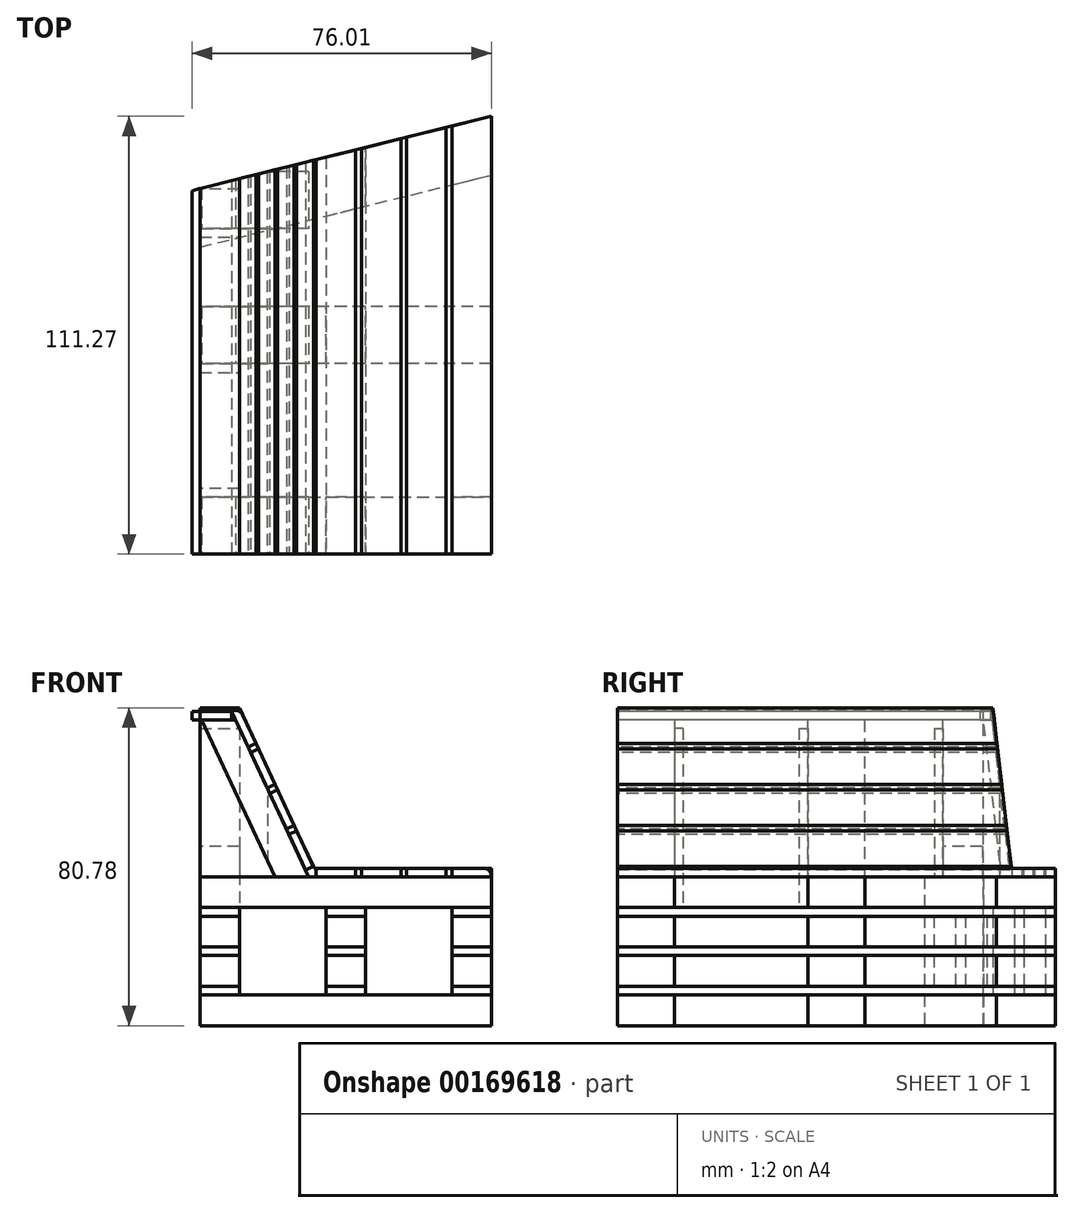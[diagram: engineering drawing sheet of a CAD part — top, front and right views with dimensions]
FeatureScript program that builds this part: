
annotation { "Feature Type Name" : "Feature", "Feature Type Description" : "" }
export const myFeature = defineFeature(function(context is Context, id is Id, definition is map)
    precondition{}
    {
        {
            assignVariable(context, id + "F0", {"name" : "h1", "anyValue" : 7.8});
        }
        {
            assignVariable(context, id + "F1", {"name" : "h2", "anyValue" : 2.2});
        }
        {
            assignVariable(context, id + "F2", {"name" : "b1", "anyValue" : 14.5});
        }
        {
            assignVariable(context, id + "F3", {"name" : "b2", "anyValue" : 10});
        }
        {
            var Q0;
            Q0=qCreatedBy(makeId("Top.planeOp"),FACE);
            var sketch = newSketch(context, id + "F4", { "sketchPlane" : qUnion([Q0])});
            skLineSegment(sketch, "E0", {"start": v(0, 0) * mm, "end": v(-33, 0) * mm});
            skLineSegment(sketch, "E1", {"start": v(-33, 0) * mm, "end": v(-33, 90) * mm});
            skLineSegment(sketch, "E2", {"start": v(0, 0) * mm, "end": v(0, -3) * mm});
            skLineSegment(sketch, "E3", {"start": v(0, -3) * mm, "end": v(42, -3) * mm});
            skLineSegment(sketch, "E4", {"start": v(42, -3) * mm, "end": v(50, -11) * mm});
            skLineSegment(sketch, "E5", {"start": v(50, -11) * mm, "end": v(85, -11) * mm});
            skLineSegment(sketch, "E6", {"start": v(0, 0) * mm, "end": v(0, 100) * mm, "construction": true});
            skLineSegment(sketch, "E7", {"start": v(42, -3) * mm, "end": v(42, 110) * mm, "construction": true});
            skFitSpline(sketch, "E8", {"points": [v(-33, 90) * mm, v(0, 100) * mm, v(42, 110) * mm, v(85, 115) * mm], "startDerivative": vector(155.67, 52.1) * mm, "endDerivative": vector(124.82, 12.6) * mm});
            skLineSegment(sketch, "E9", {"start": v(85, 115) * mm, "end": v(85, -11) * mm, "construction": true});
            skSolve(sketch);
        }
        {
            var Q0;
            Q0=sQuery(id+"F4.wireOp",EDGE,"E8");
            var Q1;
            Q1=sQuery(id+"F4.wireOp",EDGE,"E1");
            var Q2;
            Q2=sQuery(id+"F4.wireOp",EDGE,"E0");
            var Q3;
            Q3=sQuery(id+"F4.wireOp",EDGE,"E2");
            var Q4;
            Q4=sQuery(id+"F4.wireOp",EDGE,"E3");
            var Q5;
            Q5=sQuery(id+"F4.wireOp",EDGE,"E4");
            var Q6;
            Q6=sQuery(id+"F4.wireOp",EDGE,"E5");
            extrude(context, id + "F5", {"bodyType" : ToolBodyType.SURFACE, "surfaceEntities" : qUnion([Q0, Q1, Q2, Q3, Q4, Q5, Q6]), "depth" : 92 * mm});
        }
        {
            var Q0;
            Q0=qCreatedBy(makeId("Front.planeOp"),FACE);
            var sketch = newSketch(context, id + "F6", { "sketchPlane" : qUnion([Q0])});
            skLineSegment(sketch, "E10", {"start": v(-24.02, 0) * mm, "end": v(50, 0) * mm});
            skLineSegment(sketch, "E11", {"start": v(50, 0) * mm, "end": v(50, 40) * mm});
            skLineSegment(sketch, "E12", {"start": v(50, 40) * mm, "end": v(5, 40) * mm});
            skLineSegment(sketch, "E13", {"start": v(5, 40) * mm, "end": v(-14.02, 80.78) * mm});
            skLineSegment(sketch, "E14", {"start": v(-14.02, 80.78) * mm, "end": v(-24.02, 80.78) * mm});
            skLineSegment(sketch, "E15", {"start": v(-24.02, 80.78) * mm, "end": v(-24.02, 0) * mm});
            skSolve(sketch);
        }
        {
            var Q0;
            Q0 = qSketchRegion(id + "F6", true);
            var Q1;
            Q1=makeQuery(id+"F5.opExtrude","SWEPT_FACE",FACE,{"disambiguationData":[OSD([sQuery(id+"F4.wireOp",EDGE,"E8")])]});
            extrude(context, id + "F7", {"entities" : qUnion([Q0]), "endBound" : BoundingType.UP_TO_SURFACE, "oppositeDirection" : true, "endBoundEntityFace" : qUnion([Q1]), "depth" : 25 * mm});
        }
        {
            var Q0;
            Q0=qCreatedBy(makeId("Top.planeOp"),FACE);
            var sketch = newSketch(context, id + "F8", { "sketchPlane" : qUnion([Q0])});
            skLineSegment(sketch, "E16.bottom", {"start": v(-24.02, 0) * mm, "end": v(50, 0) * mm});
            skLineSegment(sketch, "E16.top", {"start": v(-24.02, 14.5) * mm, "end": v(50, 14.5) * mm});
            skLineSegment(sketch, "E16.left", {"start": v(-24.02, 0) * mm, "end": v(-24.02, 14.5) * mm});
            skLineSegment(sketch, "E16.right", {"start": v(50, 0) * mm, "end": v(50, 14.5) * mm});
            skLineSegment(sketch, "E17", {"start": v(-24.02, 92.95) * mm, "end": v(-24.02, 78.02) * mm});
            skLineSegment(sketch, "E18", {"start": v(-24.02, 78.02) * mm, "end": v(50, 96.34) * mm});
            skLineSegment(sketch, "E19", {"start": v(50, 96.34) * mm, "end": v(50, 111.27) * mm});
            skLineSegment(sketch, "E20", {"start": v(50, 111.27) * mm, "end": v(-24.02, 92.95) * mm});
            skLineSegment(sketch, "E21.bottom", {"start": v(50, 62.89) * mm, "end": v(-24.02, 62.89) * mm});
            skLineSegment(sketch, "E21.top", {"start": v(50, 48.39) * mm, "end": v(-24.02, 48.39) * mm});
            skLineSegment(sketch, "E21.left", {"start": v(50, 62.89) * mm, "end": v(50, 48.39) * mm});
            skLineSegment(sketch, "E21.right", {"start": v(-24.02, 62.89) * mm, "end": v(-24.02, 48.39) * mm});
            skPoint(sketch, "E21.middle", {"position": v(13, 55.64) * mm});
            skPoint(sketch, "E22", {"position": v(50, 55.64) * mm});
            skSolve(sketch);
        }
        {
            var Q0;
            Q0 = qSketchRegion(id + "F8", true);
            extrude(context, id + "F9", {"entities" : qUnion([Q0]), "depth" : (getVariable(context, 'h1')) * mm});
        }
        {
            var Q0;
            Q0=qCreatedBy(makeId("Front.planeOp"),FACE);
            var sketch = newSketch(context, id + "F10", { "sketchPlane" : qUnion([Q0])});
            skLineSegment(sketch, "E23.bottom", {"start": v(-14.02, 7.8) * mm, "end": v(-24.02, 7.8) * mm});
            skLineSegment(sketch, "E23.top", {"start": v(-14.02, 10) * mm, "end": v(-24.02, 10) * mm});
            skLineSegment(sketch, "E23.left", {"start": v(-14.02, 7.8) * mm, "end": v(-14.02, 10) * mm});
            skLineSegment(sketch, "E23.right", {"start": v(-24.02, 7.8) * mm, "end": v(-24.02, 10) * mm});
            skPoint(sketch, "E23.middle", {"position": v(-19.02, 8.9) * mm});
            skLineSegment(sketch, "E24.bottom", {"start": v(18, 7.8) * mm, "end": v(8, 7.8) * mm});
            skLineSegment(sketch, "E24.top", {"start": v(18, 10) * mm, "end": v(8, 10) * mm});
            skLineSegment(sketch, "E24.left", {"start": v(18, 7.8) * mm, "end": v(18, 10) * mm});
            skLineSegment(sketch, "E24.right", {"start": v(8, 7.8) * mm, "end": v(8, 10) * mm});
            skPoint(sketch, "E24.middle", {"position": v(13, 8.9) * mm});
            skLineSegment(sketch, "E25.bottom", {"start": v(50, 7.8) * mm, "end": v(40, 7.8) * mm});
            skLineSegment(sketch, "E25.top", {"start": v(50, 10) * mm, "end": v(40, 10) * mm});
            skLineSegment(sketch, "E25.left", {"start": v(50, 7.8) * mm, "end": v(50, 10) * mm});
            skLineSegment(sketch, "E25.right", {"start": v(40, 7.8) * mm, "end": v(40, 10) * mm});
            skPoint(sketch, "E25.middle", {"position": v(45, 8.9) * mm});
            skSolve(sketch);
        }
        {
            var Q0;
            Q0 = qSketchRegion(id + "F10", true);
            var Q1;
            Q1=makeQuery(id+"F5.opExtrude","SWEPT_FACE",FACE,{"disambiguationData":[OSD([sQuery(id+"F4.wireOp",EDGE,"E8")])]});
            extrude(context, id + "F11", {"entities" : qUnion([Q0]), "endBound" : BoundingType.UP_TO_SURFACE, "oppositeDirection" : true, "endBoundEntityFace" : qUnion([Q1]), "depth" : 25 * mm});
        }
        {
            var Q0;
            Q0=makeQuery(id+"F11.opExtrude","SWEPT_FACE",FACE,{"disambiguationData":[OSD([sQuery(id+"F10.wireOp",EDGE,"E25.top")])]});
            var sketch = newSketch(context, id + "F12", { "sketchPlane" : qUnion([Q0])});
            skLineSegment(sketch, "E26.bottom", {"start": v(-14.02, 48.39) * mm, "end": v(-24.02, 48.39) * mm});
            skLineSegment(sketch, "E26.top", {"start": v(-14.02, 62.89) * mm, "end": v(-24.02, 62.89) * mm});
            skLineSegment(sketch, "E26.left", {"start": v(-14.02, 48.39) * mm, "end": v(-14.02, 62.89) * mm});
            skLineSegment(sketch, "E26.right", {"start": v(-24.02, 48.39) * mm, "end": v(-24.02, 62.89) * mm});
            skPoint(sketch, "E26.middle", {"position": v(-19.02, 55.64) * mm});
            skLineSegment(sketch, "E27.bottom", {"start": v(18, 48.39) * mm, "end": v(8, 48.39) * mm});
            skLineSegment(sketch, "E27.top", {"start": v(18, 62.89) * mm, "end": v(8, 62.89) * mm});
            skLineSegment(sketch, "E27.left", {"start": v(18, 48.39) * mm, "end": v(18, 62.89) * mm});
            skLineSegment(sketch, "E27.right", {"start": v(8, 48.39) * mm, "end": v(8, 62.89) * mm});
            skPoint(sketch, "E27.middle", {"position": v(13, 55.64) * mm});
            skLineSegment(sketch, "E28.bottom", {"start": v(50, 48.39) * mm, "end": v(40, 48.39) * mm});
            skLineSegment(sketch, "E28.top", {"start": v(50, 62.89) * mm, "end": v(40, 62.89) * mm});
            skLineSegment(sketch, "E28.left", {"start": v(50, 48.39) * mm, "end": v(50, 62.89) * mm});
            skLineSegment(sketch, "E28.right", {"start": v(40, 48.39) * mm, "end": v(40, 62.89) * mm});
            skPoint(sketch, "E28.middle", {"position": v(45, 55.64) * mm});
            skLineSegment(sketch, "E29.bottom", {"start": v(-14.02, 0) * mm, "end": v(-24.02, 0) * mm});
            skLineSegment(sketch, "E29.top", {"start": v(-14.02, 14.5) * mm, "end": v(-24.02, 14.5) * mm});
            skLineSegment(sketch, "E29.left", {"start": v(-14.02, 0) * mm, "end": v(-14.02, 14.5) * mm});
            skLineSegment(sketch, "E29.right", {"start": v(-24.02, 0) * mm, "end": v(-24.02, 14.5) * mm});
            skPoint(sketch, "E29.middle", {"position": v(-19.02, 7.25) * mm});
            skLineSegment(sketch, "E30.bottom", {"start": v(18, 0) * mm, "end": v(8, 0) * mm});
            skLineSegment(sketch, "E30.top", {"start": v(18, 14.5) * mm, "end": v(8, 14.5) * mm});
            skLineSegment(sketch, "E30.left", {"start": v(18, 0) * mm, "end": v(18, 14.5) * mm});
            skLineSegment(sketch, "E30.right", {"start": v(8, 0) * mm, "end": v(8, 14.5) * mm});
            skPoint(sketch, "E30.middle", {"position": v(13, 7.25) * mm});
            skLineSegment(sketch, "E31.bottom", {"start": v(50, 0) * mm, "end": v(40, 0) * mm});
            skLineSegment(sketch, "E31.top", {"start": v(50, 14.5) * mm, "end": v(40, 14.5) * mm});
            skLineSegment(sketch, "E31.left", {"start": v(50, 0) * mm, "end": v(50, 14.5) * mm});
            skLineSegment(sketch, "E31.right", {"start": v(40, 0) * mm, "end": v(40, 14.5) * mm});
            skPoint(sketch, "E31.middle", {"position": v(45, 7.25) * mm});
            skLineSegment(sketch, "E32", {"start": v(-24.02, 78.02) * mm, "end": v(-14.02, 80.5) * mm});
            skLineSegment(sketch, "E33", {"start": v(-14.02, 80.5) * mm, "end": v(-14.02, 95.43) * mm});
            skLineSegment(sketch, "E34", {"start": v(-14.02, 95.43) * mm, "end": v(-24.02, 92.95) * mm});
            skLineSegment(sketch, "E35", {"start": v(-24.02, 92.95) * mm, "end": v(-24.02, 78.02) * mm});
            skLineSegment(sketch, "E36", {"start": v(8, 85.94) * mm, "end": v(18, 88.41) * mm});
            skLineSegment(sketch, "E37", {"start": v(18, 88.41) * mm, "end": v(18, 103.35) * mm});
            skLineSegment(sketch, "E38", {"start": v(18, 103.35) * mm, "end": v(8, 100.88) * mm});
            skLineSegment(sketch, "E39", {"start": v(8, 100.88) * mm, "end": v(8, 85.94) * mm});
            skLineSegment(sketch, "E40", {"start": v(40, 93.86) * mm, "end": v(50, 96.34) * mm});
            skLineSegment(sketch, "E41", {"start": v(50, 96.34) * mm, "end": v(50, 111.27) * mm});
            skLineSegment(sketch, "E42", {"start": v(50, 111.27) * mm, "end": v(40, 108.8) * mm});
            skLineSegment(sketch, "E43", {"start": v(40, 108.8) * mm, "end": v(40, 93.86) * mm});
            skSolve(sketch);
        }
        {
            var Q0;
            Q0=makeQuery(id+"F11.opExtrude","SWEPT_BODY",BODY,{"disambiguationData":[OSD([sQuery(id+"F10.wireOp",EDGE,"E25.bottom"),sQuery(id+"F10.wireOp",EDGE,"E25.top"),sQuery(id+"F10.wireOp",EDGE,"E25.left"),sQuery(id+"F10.wireOp",EDGE,"E25.right")])]});
            var Q1;
            Q1=makeQuery(id+"F11.opExtrude","SWEPT_BODY",BODY,{"disambiguationData":[OSD([sQuery(id+"F10.wireOp",EDGE,"E24.bottom"),sQuery(id+"F10.wireOp",EDGE,"E24.top"),sQuery(id+"F10.wireOp",EDGE,"E24.left"),sQuery(id+"F10.wireOp",EDGE,"E24.right")])]});
            var Q2;
            Q2=makeQuery(id+"F11.opExtrude","SWEPT_BODY",BODY,{"disambiguationData":[OSD([sQuery(id+"F10.wireOp",EDGE,"E23.bottom"),sQuery(id+"F10.wireOp",EDGE,"E23.top"),sQuery(id+"F10.wireOp",EDGE,"E23.left"),sQuery(id+"F10.wireOp",EDGE,"E23.right")])]});
            transform(context, id + "F13", {"entities" : qUnion([Q0, Q1, Q2]), "transformType" : TransformType.TRANSLATION_3D, "dx" : 0 * mm, "dy" : 0 * mm, "dz" : (getVariable(context, 'h1') + getVariable(context, 'h2')) * mm, "makeCopy" : true});
        }
        {
            var Q0;
            Q0=makeQuery(id+"Fk0cpU2CD6sY0ll_8.opPattern","COPY",BODY,{"derivedFrom":makeQuery(id+"F9.opExtrude","SWEPT_BODY",BODY,{"disambiguationData":[OSD([sQuery(id+"F8.wireOp",EDGE,"E16.bottom"),sQuery(id+"F8.wireOp",EDGE,"E16.top"),sQuery(id+"F8.wireOp",EDGE,"E16.left"),sQuery(id+"F8.wireOp",EDGE,"E16.right")])]}),"instanceName":"1"});
            var Q1;
            Q1=makeQuery(id+"Fk0cpU2CD6sY0ll_8.opPattern","COPY",BODY,{"derivedFrom":makeQuery(id+"F9.opExtrude","SWEPT_BODY",BODY,{"disambiguationData":[OSD([sQuery(id+"F8.wireOp",EDGE,"E21.bottom"),sQuery(id+"F8.wireOp",EDGE,"E21.top"),sQuery(id+"F8.wireOp",EDGE,"E21.left"),sQuery(id+"F8.wireOp",EDGE,"E21.right")])]}),"instanceName":"1"});
            var Q2;
            Q2=makeQuery(id+"Fk0cpU2CD6sY0ll_8.opPattern","COPY",BODY,{"derivedFrom":makeQuery(id+"F9.opExtrude","SWEPT_BODY",BODY,{"disambiguationData":[OSD([sQuery(id+"F8.wireOp",EDGE,"E17"),sQuery(id+"F8.wireOp",EDGE,"E18"),sQuery(id+"F8.wireOp",EDGE,"E19"),sQuery(id+"F8.wireOp",EDGE,"E20")])]}),"instanceName":"1"});
            var Q3;
            Q3=makeQuery(id+"F13.opPattern","COPY",BODY,{"derivedFrom":makeQuery(id+"F11.opExtrude","SWEPT_BODY",BODY,{"disambiguationData":[OSD([sQuery(id+"F10.wireOp",EDGE,"E25.bottom"),sQuery(id+"F10.wireOp",EDGE,"E25.top"),sQuery(id+"F10.wireOp",EDGE,"E25.left"),sQuery(id+"F10.wireOp",EDGE,"E25.right")])]}),"instanceName":"1"});
            var Q4;
            Q4=makeQuery(id+"F13.opPattern","COPY",BODY,{"derivedFrom":makeQuery(id+"F11.opExtrude","SWEPT_BODY",BODY,{"disambiguationData":[OSD([sQuery(id+"F10.wireOp",EDGE,"E24.bottom"),sQuery(id+"F10.wireOp",EDGE,"E24.top"),sQuery(id+"F10.wireOp",EDGE,"E24.left"),sQuery(id+"F10.wireOp",EDGE,"E24.right")])]}),"instanceName":"1"});
            var Q5;
            Q5=makeQuery(id+"F13.opPattern","COPY",BODY,{"derivedFrom":makeQuery(id+"F11.opExtrude","SWEPT_BODY",BODY,{"disambiguationData":[OSD([sQuery(id+"F10.wireOp",EDGE,"E23.bottom"),sQuery(id+"F10.wireOp",EDGE,"E23.top"),sQuery(id+"F10.wireOp",EDGE,"E23.left"),sQuery(id+"F10.wireOp",EDGE,"E23.right")])]}),"instanceName":"1"});
            transform(context, id + "F14", {"entities" : qUnion([Q0, Q1, Q2, Q3, Q4, Q5]), "transformType" : TransformType.TRANSLATION_3D, "dx" : 0 * mm, "dy" : 0 * mm, "dz" : (getVariable(context, 'h1') + getVariable(context, 'h2')) * mm, "makeCopy" : true});
        }
        {
            var Q0;
            Q0 = qSketchRegion(id + "F12", true);
            extrude(context, id + "F15", {"entities" : qUnion([Q0]), "depth" : (getVariable(context, 'h1')) * mm});
        }
        {
            var Q0;
            Q0=makeQuery(id+"F15.opExtrude","SWEPT_BODY",BODY,{"disambiguationData":[OSD([sQuery(id+"F12.wireOp",EDGE,"E31.bottom"),sQuery(id+"F12.wireOp",EDGE,"E31.top"),sQuery(id+"F12.wireOp",EDGE,"E31.left"),sQuery(id+"F12.wireOp",EDGE,"E31.right")])]});
            var Q1;
            Q1=makeQuery(id+"F15.opExtrude","SWEPT_BODY",BODY,{"disambiguationData":[OSD([sQuery(id+"F12.wireOp",EDGE,"E30.bottom"),sQuery(id+"F12.wireOp",EDGE,"E30.top"),sQuery(id+"F12.wireOp",EDGE,"E30.left"),sQuery(id+"F12.wireOp",EDGE,"E30.right")])]});
            var Q2;
            Q2=makeQuery(id+"F15.opExtrude","SWEPT_BODY",BODY,{"disambiguationData":[OSD([sQuery(id+"F12.wireOp",EDGE,"E29.bottom"),sQuery(id+"F12.wireOp",EDGE,"E29.top"),sQuery(id+"F12.wireOp",EDGE,"E29.left"),sQuery(id+"F12.wireOp",EDGE,"E29.right")])]});
            var Q3;
            Q3=makeQuery(id+"F15.opExtrude","SWEPT_BODY",BODY,{"disambiguationData":[OSD([sQuery(id+"F12.wireOp",EDGE,"E26.bottom"),sQuery(id+"F12.wireOp",EDGE,"E26.top"),sQuery(id+"F12.wireOp",EDGE,"E26.left"),sQuery(id+"F12.wireOp",EDGE,"E26.right")])]});
            var Q4;
            Q4=makeQuery(id+"F15.opExtrude","SWEPT_BODY",BODY,{"disambiguationData":[OSD([sQuery(id+"F12.wireOp",EDGE,"E27.bottom"),sQuery(id+"F12.wireOp",EDGE,"E27.top"),sQuery(id+"F12.wireOp",EDGE,"E27.left"),sQuery(id+"F12.wireOp",EDGE,"E27.right")])]});
            var Q5;
            Q5=makeQuery(id+"F15.opExtrude","SWEPT_BODY",BODY,{"disambiguationData":[OSD([sQuery(id+"F12.wireOp",EDGE,"E28.bottom"),sQuery(id+"F12.wireOp",EDGE,"E28.top"),sQuery(id+"F12.wireOp",EDGE,"E28.left"),sQuery(id+"F12.wireOp",EDGE,"E28.right")])]});
            var Q6;
            Q6=makeQuery(id+"F15.opExtrude","SWEPT_BODY",BODY,{"disambiguationData":[OSD([sQuery(id+"F12.wireOp",EDGE,"E32"),sQuery(id+"F12.wireOp",EDGE,"E33"),sQuery(id+"F12.wireOp",EDGE,"E34"),sQuery(id+"F12.wireOp",EDGE,"E35")])]});
            var Q7;
            Q7=makeQuery(id+"F15.opExtrude","SWEPT_BODY",BODY,{"disambiguationData":[OSD([sQuery(id+"F12.wireOp",EDGE,"E36"),sQuery(id+"F12.wireOp",EDGE,"E37"),sQuery(id+"F12.wireOp",EDGE,"E38"),sQuery(id+"F12.wireOp",EDGE,"E39")])]});
            var Q8;
            Q8=makeQuery(id+"F15.opExtrude","SWEPT_BODY",BODY,{"disambiguationData":[OSD([sQuery(id+"F12.wireOp",EDGE,"E40"),sQuery(id+"F12.wireOp",EDGE,"E41"),sQuery(id+"F12.wireOp",EDGE,"E42"),sQuery(id+"F12.wireOp",EDGE,"E43")])]});
            transform(context, id + "F16", {"entities" : qUnion([Q0, Q1, Q2, Q3, Q4, Q5, Q6, Q7, Q8]), "transformType" : TransformType.TRANSLATION_3D, "dx" : 0 * mm, "dy" : 0 * mm, "dz" : (getVariable(context, 'h1') + getVariable(context, 'h2')) * mm, "makeCopy" : true});
        }
        {
            var Q0;
            Q0=makeQuery(id+"F9.opExtrude","SWEPT_BODY",BODY,{"disambiguationData":[OSD([sQuery(id+"F8.wireOp",EDGE,"E16.bottom"),sQuery(id+"F8.wireOp",EDGE,"E16.top"),sQuery(id+"F8.wireOp",EDGE,"E16.left"),sQuery(id+"F8.wireOp",EDGE,"E16.right")])]});
            var Q1;
            Q1=makeQuery(id+"F9.opExtrude","SWEPT_BODY",BODY,{"disambiguationData":[OSD([sQuery(id+"F8.wireOp",EDGE,"E21.bottom"),sQuery(id+"F8.wireOp",EDGE,"E21.top"),sQuery(id+"F8.wireOp",EDGE,"E21.left"),sQuery(id+"F8.wireOp",EDGE,"E21.right")])]});
            var Q2;
            Q2=makeQuery(id+"F9.opExtrude","SWEPT_BODY",BODY,{"disambiguationData":[OSD([sQuery(id+"F8.wireOp",EDGE,"E17"),sQuery(id+"F8.wireOp",EDGE,"E18"),sQuery(id+"F8.wireOp",EDGE,"E19"),sQuery(id+"F8.wireOp",EDGE,"E20")])]});
            transform(context, id + "F17", {"entities" : qUnion([Q0, Q1, Q2]), "transformType" : TransformType.TRANSLATION_3D, "dx" : 0 * mm, "dy" : 0 * mm, "dz" : (3 * (getVariable(context, 'h1') + getVariable(context, 'h2'))) * mm, "makeCopy" : true});
        }
        {
            var Q0;
            Q0=qCreatedBy(makeId("Front.planeOp"),FACE);
            var sketch = newSketch(context, id + "F18", { "sketchPlane" : qUnion([Q0])});
            skLineSegment(sketch, "E44.bottom", {"start": v(50, 37.8) * mm, "end": v(40, 37.8) * mm});
            skLineSegment(sketch, "E44.top", {"start": v(50, 40) * mm, "end": v(40, 40) * mm});
            skLineSegment(sketch, "E44.left", {"start": v(50, 37.8) * mm, "end": v(50, 40) * mm});
            skLineSegment(sketch, "E44.right", {"start": v(40, 37.8) * mm, "end": v(40, 40) * mm});
            skLineSegment(sketch, "E45.bottom", {"start": v(38.5, 37.8) * mm, "end": v(28.5, 37.8) * mm});
            skLineSegment(sketch, "E45.top", {"start": v(38.5, 40) * mm, "end": v(28.5, 40) * mm});
            skLineSegment(sketch, "E45.left", {"start": v(38.5, 37.8) * mm, "end": v(38.5, 40) * mm});
            skLineSegment(sketch, "E45.right", {"start": v(28.5, 37.8) * mm, "end": v(28.5, 40) * mm});
            skLineSegment(sketch, "E46.bottom", {"start": v(27, 37.8) * mm, "end": v(17, 37.8) * mm});
            skLineSegment(sketch, "E46.top", {"start": v(27, 40) * mm, "end": v(17, 40) * mm});
            skLineSegment(sketch, "E46.left", {"start": v(27, 37.8) * mm, "end": v(27, 40) * mm});
            skLineSegment(sketch, "E46.right", {"start": v(17, 37.8) * mm, "end": v(17, 40) * mm});
            skLineSegment(sketch, "E47.bottom", {"start": v(5.5, 37.8) * mm, "end": v(15.5, 37.8) * mm});
            skLineSegment(sketch, "E47.top", {"start": v(5.5, 40) * mm, "end": v(15.5, 40) * mm});
            skLineSegment(sketch, "E47.left", {"start": v(5.5, 37.8) * mm, "end": v(5.5, 40) * mm});
            skLineSegment(sketch, "E47.right", {"start": v(15.5, 37.8) * mm, "end": v(15.5, 40) * mm});
            skSolve(sketch);
        }
        {
            var Q0;
            Q0 = qSketchRegion(id + "F18", true);
            var Q1;
            Q1=makeQuery(id+"F5.opExtrude","SWEPT_FACE",FACE,{"disambiguationData":[OSD([sQuery(id+"F4.wireOp",EDGE,"E8")])]});
            extrude(context, id + "F19", {"entities" : qUnion([Q0]), "endBound" : BoundingType.UP_TO_SURFACE, "oppositeDirection" : true, "endBoundEntityFace" : qUnion([Q1]), "depth" : 25 * mm});
        }
        {
            var Q0;
            Q0=qCreatedBy(makeId("Front.planeOp"),FACE);
            var sketch = newSketch(context, id + "F20", { "sketchPlane" : qUnion([Q0])});
            skLineSegment(sketch, "E48", {"start": v(-14.02, 80.78) * mm, "end": v(-9.8, 71.72) * mm});
            skLineSegment(sketch, "E49", {"start": v(-9.8, 71.72) * mm, "end": v(-11.79, 70.8) * mm});
            skLineSegment(sketch, "E50", {"start": v(-11.79, 70.8) * mm, "end": v(-16.01, 79.85) * mm});
            skLineSegment(sketch, "E51", {"start": v(-16.01, 79.85) * mm, "end": v(-14.02, 80.78) * mm});
            skLineSegment(sketch, "E52", {"start": v(-9.16, 70.36) * mm, "end": v(-4.93, 61.3) * mm});
            skLineSegment(sketch, "E53", {"start": v(-4.93, 61.3) * mm, "end": v(-6.93, 60.37) * mm});
            skLineSegment(sketch, "E54", {"start": v(-6.93, 60.37) * mm, "end": v(-11.15, 69.43) * mm});
            skLineSegment(sketch, "E55", {"start": v(-11.15, 69.43) * mm, "end": v(-9.16, 70.36) * mm});
            skLineSegment(sketch, "E56", {"start": v(-6.3, 59) * mm, "end": v(-2.07, 49.95) * mm});
            skLineSegment(sketch, "E57", {"start": v(-2.07, 49.95) * mm, "end": v(-0.07, 50.88) * mm});
            skLineSegment(sketch, "E58", {"start": v(-0.07, 50.88) * mm, "end": v(-4.3, 59.94) * mm});
            skLineSegment(sketch, "E59", {"start": v(-4.3, 59.94) * mm, "end": v(-6.3, 59) * mm});
            skLineSegment(sketch, "E60", {"start": v(0.56, 49.52) * mm, "end": v(4.79, 40.45) * mm});
            skLineSegment(sketch, "E61", {"start": v(4.79, 40.45) * mm, "end": v(2.8, 39.52) * mm});
            skLineSegment(sketch, "E62", {"start": v(2.8, 39.52) * mm, "end": v(-1.43, 48.59) * mm});
            skLineSegment(sketch, "E63", {"start": v(-1.43, 48.59) * mm, "end": v(0.56, 49.52) * mm});
            skSolve(sketch);
        }
        {
            var Q0;
            Q0 = qSketchRegion(id + "F20", true);
            var Q1;
            Q1=makeQuery(id+"F5.opExtrude","SWEPT_FACE",FACE,{"disambiguationData":[OSD([sQuery(id+"F4.wireOp",EDGE,"E8")])]});
            extrude(context, id + "F21", {"entities" : qUnion([Q0]), "endBound" : BoundingType.UP_TO_SURFACE, "oppositeDirection" : true, "endBoundEntityFace" : qUnion([Q1]), "depth" : 25 * mm});
        }
        {
            var Q0;
            Q0=qCreatedBy(makeId("Front.planeOp"),FACE);
            var sketch = newSketch(context, id + "F22", { "sketchPlane" : qUnion([Q0])});
            skLineSegment(sketch, "E64", {"start": v(-5, 37.8) * mm, "end": v(3.6, 37.8) * mm});
            skLineSegment(sketch, "E65", {"start": v(3.6, 37.8) * mm, "end": v(-14.99, 77.65) * mm});
            skLineSegment(sketch, "E66", {"start": v(-14.99, 77.65) * mm, "end": v(-23.6, 77.65) * mm});
            skLineSegment(sketch, "E67", {"start": v(-23.6, 77.65) * mm, "end": v(-5, 37.8) * mm});
            skSolve(sketch);
        }
        {
            var Q0;
            Q0 = qSketchRegion(id + "F22", true);
            extrude(context, id + "F23", {"entities" : qUnion([Q0]), "oppositeDirection" : true, "depth" : (getVariable(context, 'b1')) * mm});
        }
        {
            var Q0;
            Q0=makeQuery(id+"F17.opPattern","COPY",FACE,{"derivedFrom":makeQuery(id+"F9.opExtrude","SWEPT_FACE",FACE,{"disambiguationData":[OSD([sQuery(id+"F8.wireOp",EDGE,"E21.top")])]}),"instanceName":"1"});
            var sketch = newSketch(context, id + "F24", { "sketchPlane" : qUnion([Q0])});
            skLineSegment(sketch, "E68", {"start": v(-5, 37.8) * mm, "end": v(3.6, 37.8) * mm});
            skLineSegment(sketch, "E69", {"start": v(3.6, 37.8) * mm, "end": v(-14.99, 77.65) * mm});
            skLineSegment(sketch, "E70", {"start": v(-14.99, 77.65) * mm, "end": v(-23.6, 77.65) * mm});
            skLineSegment(sketch, "E71", {"start": v(-23.6, 77.65) * mm, "end": v(-5, 37.8) * mm});
            skSolve(sketch);
        }
        {
            var Q0;
            Q0=makeQuery(id+"F24.imprint","IMPRINT",FACE,{"disambiguationData":[TD([[makeQuery(id+"F24.imprint","IMPRINT",EDGE,{"derivedFrom":sQuery(id+"F24.wireOp",EDGE,"E68")}),-1.0]])]});
            extrude(context, id + "F25", {"entities" : qUnion([Q0]), "oppositeDirection" : true, "depth" : (getVariable(context, 'b1')) * mm});
        }
        {
            var Q0;
            Q0=makeQuery(id+"F17.opPattern","COPY",FACE,{"derivedFrom":makeQuery(id+"F9.opExtrude","CAP_FACE",FACE,{"disambiguationData":[OSD([sQuery(id+"F8.wireOp",EDGE,"E17"),sQuery(id+"F8.wireOp",EDGE,"E18"),sQuery(id+"F8.wireOp",EDGE,"E19"),sQuery(id+"F8.wireOp",EDGE,"E20")])],"isStart":false}),"instanceName":"1"});
            var sketch = newSketch(context, id + "F26", { "sketchPlane" : qUnion([Q0])});
            skLineSegment(sketch, "E72", {"start": v(-5, 48.39) * mm, "end": v(-5, 82.72) * mm, "construction": true});
            skSolve(sketch);
        }
        {
            var Q0;
            Q0=makeQuery(id+"F25.opExtrude","SWEPT_BODY",BODY,{"disambiguationData":[OSD([sQuery(id+"F24.wireOp",EDGE,"E68"),sQuery(id+"F24.wireOp",EDGE,"E69"),sQuery(id+"F24.wireOp",EDGE,"E70"),sQuery(id+"F24.wireOp",EDGE,"E71")])]});
            var Q1;
            Q1=sQuery(id+"F26.wireOp",EDGE,"E72");
            transform(context, id + "F27", {"entities" : qUnion([Q0]), "transformType" : TransformType.TRANSLATION_ENTITY, "oppositeDirectionEntity" : false, "transformLine" : qUnion([Q1]), "makeCopy" : true});
        }
        {
            var Q0;
            Q0=makeQuery(id+"F23.opExtrude","CAP_FACE",FACE,{"disambiguationData":[OSD([sQuery(id+"F22.wireOp",EDGE,"E64"),sQuery(id+"F22.wireOp",EDGE,"E65"),sQuery(id+"F22.wireOp",EDGE,"E66"),sQuery(id+"F22.wireOp",EDGE,"E67")])],"isStart":false});
            var sketch = newSketch(context, id + "F28", { "sketchPlane" : qUnion([Q0])});
            skLineSegment(sketch, "E73.bottom", {"start": v(14.02, 75.58) * mm, "end": v(24.02, 75.58) * mm});
            skLineSegment(sketch, "E73.top", {"start": v(14.02, 30) * mm, "end": v(24.02, 30) * mm});
            skLineSegment(sketch, "E73.left", {"start": v(14.02, 75.58) * mm, "end": v(14.02, 30) * mm});
            skLineSegment(sketch, "E73.right", {"start": v(24.02, 75.58) * mm, "end": v(24.02, 30) * mm});
            skSolve(sketch);
        }
        {
            var Q0;
            Q0 = qSketchRegion(id + "F28", true);
            extrude(context, id + "F29", {"entities" : qUnion([Q0]), "depth" : (getVariable(context, 'h2')) * mm});
        }
        {
            var Q0;
            Q0=makeQuery(id+"F17.opPattern","COPY",FACE,{"derivedFrom":makeQuery(id+"F9.opExtrude","SWEPT_FACE",FACE,{"disambiguationData":[OSD([sQuery(id+"F8.wireOp",EDGE,"E21.top")])]}),"instanceName":"1"});
            var sketch = newSketch(context, id + "F30", { "sketchPlane" : qUnion([Q0])});
            skLineSegment(sketch, "E74.bottom", {"start": v(-24.02, 75.58) * mm, "end": v(-14.02, 75.58) * mm});
            skLineSegment(sketch, "E74.top", {"start": v(-24.02, 30) * mm, "end": v(-14.02, 30) * mm});
            skLineSegment(sketch, "E74.left", {"start": v(-24.02, 75.58) * mm, "end": v(-24.02, 30) * mm});
            skLineSegment(sketch, "E74.right", {"start": v(-14.02, 75.58) * mm, "end": v(-14.02, 30) * mm});
            skSolve(sketch);
        }
        {
            var Q0;
            Q0 = qSketchRegion(id + "F30", true);
            extrude(context, id + "F31", {"entities" : qUnion([Q0]), "depth" : (getVariable(context, 'h2')) * mm});
        }
        {
            var Q0;
            Q0=makeQuery(id+"F27.opPattern","COPY",FACE,{"derivedFrom":makeQuery(id+"F25.opExtrude","CAP_FACE",FACE,{"disambiguationData":[OSD([sQuery(id+"F24.wireOp",EDGE,"E68"),sQuery(id+"F24.wireOp",EDGE,"E69"),sQuery(id+"F24.wireOp",EDGE,"E70"),sQuery(id+"F24.wireOp",EDGE,"E71")])],"isStart":true}),"instanceName":"1"});
            var sketch = newSketch(context, id + "F32", { "sketchPlane" : qUnion([Q0])});
            skLineSegment(sketch, "E75.bottom", {"start": v(-24.02, 75.58) * mm, "end": v(-14.02, 75.58) * mm});
            skLineSegment(sketch, "E75.top", {"start": v(-24.02, 37.8) * mm, "end": v(-14.02, 37.8) * mm});
            skLineSegment(sketch, "E75.left", {"start": v(-24.02, 75.58) * mm, "end": v(-24.02, 37.8) * mm});
            skLineSegment(sketch, "E75.right", {"start": v(-14.02, 75.58) * mm, "end": v(-14.02, 37.8) * mm});
            skSolve(sketch);
        }
        {
            var Q0;
            Q0 = qSketchRegion(id + "F32", true);
            extrude(context, id + "F33", {"entities" : qUnion([Q0]), "depth" : (getVariable(context, 'h2')) * mm});
        }
        {
            var Q0;
            Q0=makeQuery(id+"F33.opExtrude","CAP_FACE",FACE,{"disambiguationData":[OSD([sQuery(id+"F32.wireOp",EDGE,"E75.bottom"),sQuery(id+"F32.wireOp",EDGE,"E75.top"),sQuery(id+"F32.wireOp",EDGE,"E75.left"),sQuery(id+"F32.wireOp",EDGE,"E75.right")])],"isStart":true});
            var sketch = newSketch(context, id + "F34", { "sketchPlane" : qUnion([Q0])});
            skLineSegment(sketch, "E76.bottom", {"start": v(14.02, 45.6) * mm, "end": v(24.02, 45.6) * mm});
            skLineSegment(sketch, "E76.top", {"start": v(14.02, 37.8) * mm, "end": v(24.02, 37.8) * mm});
            skLineSegment(sketch, "E76.left", {"start": v(14.02, 45.6) * mm, "end": v(14.02, 37.8) * mm});
            skLineSegment(sketch, "E76.right", {"start": v(24.02, 45.6) * mm, "end": v(24.02, 37.8) * mm});
            skSolve(sketch);
        }
        {
            var Q0;
            Q0=makeQuery(id+"F34.imprint","IMPRINT",FACE,{"disambiguationData":[TD([[makeQuery(id+"F34.imprint","IMPRINT",EDGE,{"derivedFrom":sQuery(id+"F34.wireOp",EDGE,"E76.bottom")}),-1.0]])]});
            extrude(context, id + "F35", {"entities" : qUnion([Q0]), "depth" : (getVariable(context, 'b2')) * mm});
        }
        {
            var Q0;
            Q0=makeQuery(id+"F21.opExtrude","SWEPT_EDGE",EDGE,{"disambiguationData":[OSD([sQuery(id+"F20.wireOp",EDGE,"E48"),sQuery(id+"F20.wireOp",EDGE,"E51")])]});
            var Q1;
            Q1=makeQuery(id+"F38.opExtrude","SWEPT_EDGE",EDGE,{"disambiguationData":[OSD([sQuery(id+"F37.wireOp",EDGE,"E77.bottom"),sQuery(id+"F37.wireOp",EDGE,"E77.left")])]});
            var Q2;
            Q2=makeQuery(id+"F19.opExtrude","SWEPT_EDGE",EDGE,{"disambiguationData":[OSD([sQuery(id+"F18.wireOp",EDGE,"E44.top"),sQuery(id+"F18.wireOp",EDGE,"E44.left")])]});
            fillet(context, id + "F36", {"entities" : qUnion([Q0, Q1, Q2]), "radius" : 2 * mm, "tangentPropagation" : true, "allowEdgeOverflow" : false});
        }
        {
            var Q0;
            Q0=qCreatedBy(makeId("Front.planeOp"),FACE);
            var sketch = newSketch(context, id + "F37", { "sketchPlane" : qUnion([Q0])});
            skLineSegment(sketch, "E77.bottom", {"start": v(-26.01, 79.85) * mm, "end": v(-16.01, 79.85) * mm});
            skLineSegment(sketch, "E77.top", {"start": v(-26.01, 77.65) * mm, "end": v(-16.01, 77.65) * mm});
            skLineSegment(sketch, "E77.left", {"start": v(-26.01, 79.85) * mm, "end": v(-26.01, 77.65) * mm});
            skLineSegment(sketch, "E77.right", {"start": v(-16.01, 79.85) * mm, "end": v(-16.01, 77.65) * mm});
            skSolve(sketch);
        }
        {
            var Q0;
            Q0 = qSketchRegion(id + "F37", true);
            var Q1;
            Q1=makeQuery(id+"F5.opExtrude","SWEPT_FACE",FACE,{"disambiguationData":[OSD([sQuery(id+"F4.wireOp",EDGE,"E8")])]});
            extrude(context, id + "F38", {"entities" : qUnion([Q0]), "endBound" : BoundingType.UP_TO_SURFACE, "oppositeDirection" : true, "endBoundEntityFace" : qUnion([Q1]), "depth" : 25 * mm});
        }
        {
            var Q0;
            Q0=makeQuery(id+"F9.opExtrude","CAP_FACE",FACE,{"disambiguationData":[OSD([sQuery(id+"F8.wireOp",EDGE,"E17"),sQuery(id+"F8.wireOp",EDGE,"E18"),sQuery(id+"F8.wireOp",EDGE,"E19"),sQuery(id+"F8.wireOp",EDGE,"E20")])],"isStart":true});
            var sketch = newSketch(context, id + "F39", { "sketchPlane" : qUnion([Q0])});
            skLineSegment(sketch, "E78", {"start": v(-24.02, -92.95) * mm, "end": v(50, -111.27) * mm});
            skLineSegment(sketch, "E79", {"start": v(50, -111.27) * mm, "end": v(50, -115.44) * mm});
            skLineSegment(sketch, "E80", {"start": v(50, -115.44) * mm, "end": v(-24.02, -97.12) * mm});
            skLineSegment(sketch, "E81", {"start": v(-24.02, -97.12) * mm, "end": v(-24.02, -92.95) * mm});
            skSolve(sketch);
        }
        {
            var Q0;
            Q0 = qSketchRegion(id + "F39", true);
            var Q1;
            Q1=makeQuery(id+"F38.opExtrude","SWEPT_FACE",FACE,{"disambiguationData":[OSD([sQuery(id+"F37.wireOp",EDGE,"E77.bottom")])]});
            extrude(context, id + "F40", {"entities" : qUnion([Q0]), "operationType" : NewBodyOperationType.REMOVE, "endBound" : BoundingType.THROUGH_ALL, "oppositeDirection" : true, "endBoundEntityFace" : qUnion([Q1]), "depth" : 25 * mm});
        }
    });
